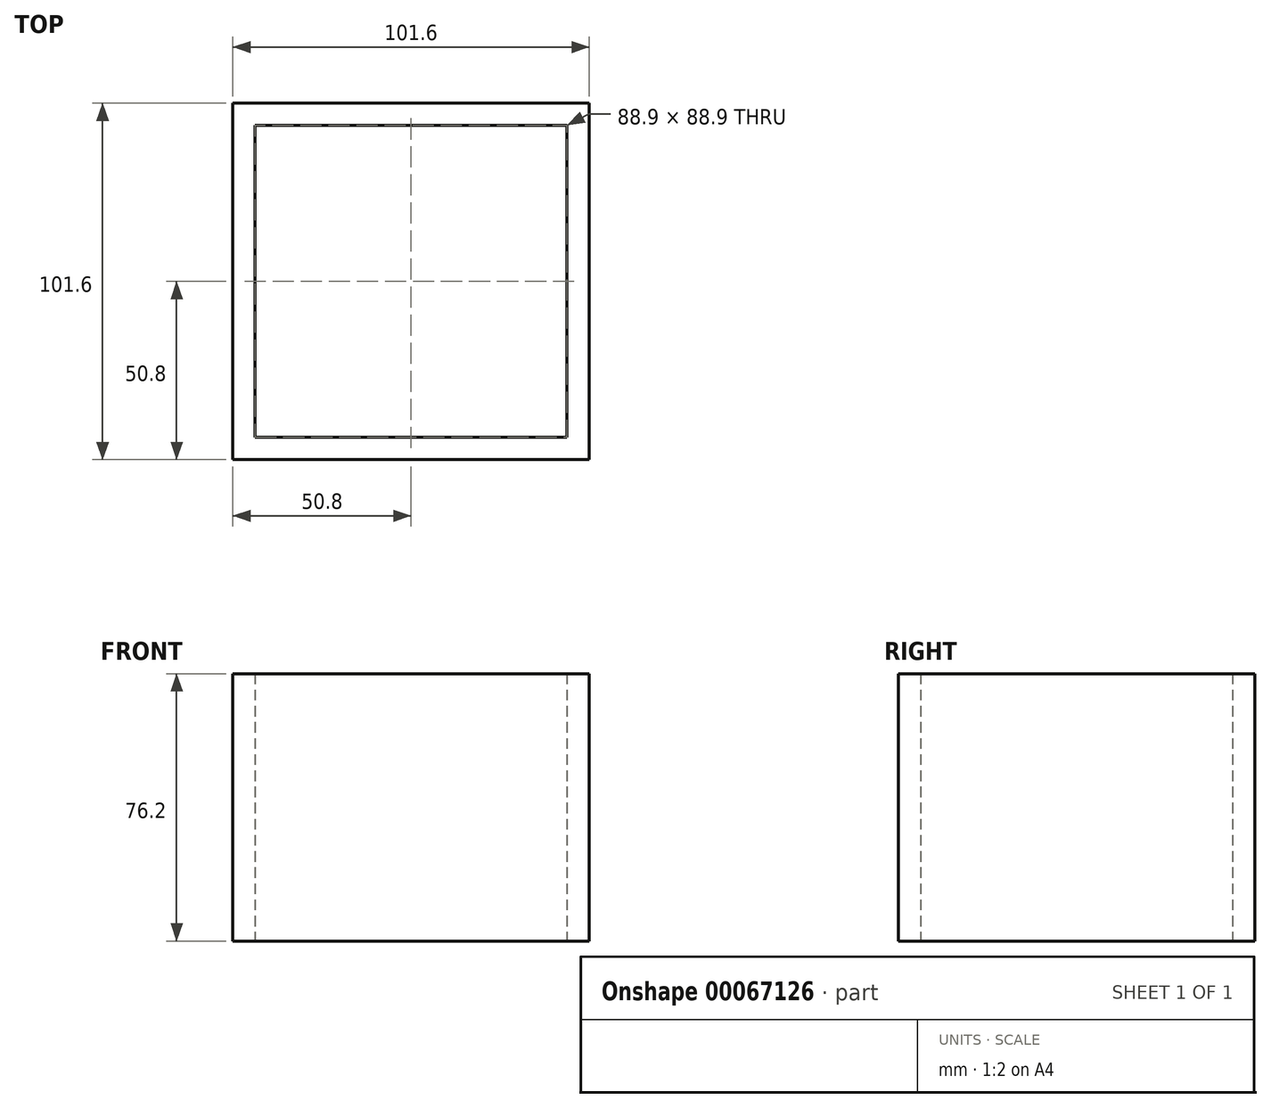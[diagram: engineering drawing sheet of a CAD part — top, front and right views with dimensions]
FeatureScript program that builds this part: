
annotation { "Feature Type Name" : "Feature", "Feature Type Description" : "" }
export const myFeature = defineFeature(function(context is Context, id is Id, definition is map)
    precondition{}
    {
        {
            var Q0;
            Q0=qCreatedBy(makeId("Top.planeOp"),FACE);
            var sketch = newSketch(context, id + "F0", { "sketchPlane" : qUnion([Q0])});
            skPoint(sketch, "E0.MirrorCS.end.orphan", {"position": v(0, 114.3) * mm});
            skPoint(sketch, "E0.MirrorCS.start.orphan", {"position": v(38.1, 114.3) * mm});
            skLineSegment(sketch, "E1", {"start": v(50.8, 50.8) * mm, "end": v(50.8, -50.8) * mm});
            skLineSegment(sketch, "E2", {"start": v(50.8, -50.8) * mm, "end": v(-50.8, -50.8) * mm});
            skPoint(sketch, "E3.end.orphan", {"position": v(0, 50.8) * mm});
            skLineSegment(sketch, "E4", {"start": v(50.8, 50.8) * mm, "end": v(0, 50.8) * mm});
            skLineSegment(sketch, "E5", {"start": v(0, 50.8) * mm, "end": v(-50.8, 50.8) * mm});
            skLineSegment(sketch, "E6", {"start": v(-50.8, 50.8) * mm, "end": v(-50.8, -50.8) * mm});
            skLineSegment(sketch, "E7", {"start": v(0, 44.45) * mm, "end": v(44.45, 44.45) * mm});
            skLineSegment(sketch, "E8", {"start": v(0, 44.45) * mm, "end": v(-44.45, 44.45) * mm});
            skLineSegment(sketch, "E9", {"start": v(44.45, 0) * mm, "end": v(44.45, 44.45) * mm});
            skLineSegment(sketch, "E10.MirrorCS", {"start": v(0, -44.45) * mm, "end": v(44.45, -44.45) * mm});
            skLineSegment(sketch, "E11.MirrorCS", {"start": v(0, -44.45) * mm, "end": v(-44.45, -44.45) * mm});
            skLineSegment(sketch, "E12.MirrorCS", {"start": v(44.45, 0) * mm, "end": v(44.45, -44.45) * mm});
            skLineSegment(sketch, "E13.MirrorCS", {"start": v(-44.45, 0) * mm, "end": v(-44.45, 44.45) * mm});
            skLineSegment(sketch, "E14.MirrorCS", {"start": v(-44.45, 0) * mm, "end": v(-44.45, -44.45) * mm});
            skPoint(sketch, "E15.orphan", {"position": v(-50.8, 44.45) * mm});
            skPoint(sketch, "E16.orphan", {"position": v(-50.8, -44.45) * mm});
            skPoint(sketch, "E17.orphan", {"position": v(50.8, -44.45) * mm});
            skPoint(sketch, "E18.orphan", {"position": v(50.8, 44.45) * mm});
            skSolve(sketch);
        }
        {
            var Q0;
            Q0=makeQuery(id+"F0.imprint","IMPRINT",FACE,{"disambiguationData":[TD([[makeQuery(id+"F0.imprint","IMPRINT",EDGE,{"derivedFrom":sQuery(id+"F0.wireOp",EDGE,"E1")}),-1.0]])]});
            extrude(context, id + "F1", {"entities" : qUnion([Q0]), "depth" : 76.2 * mm});
        }
    });
